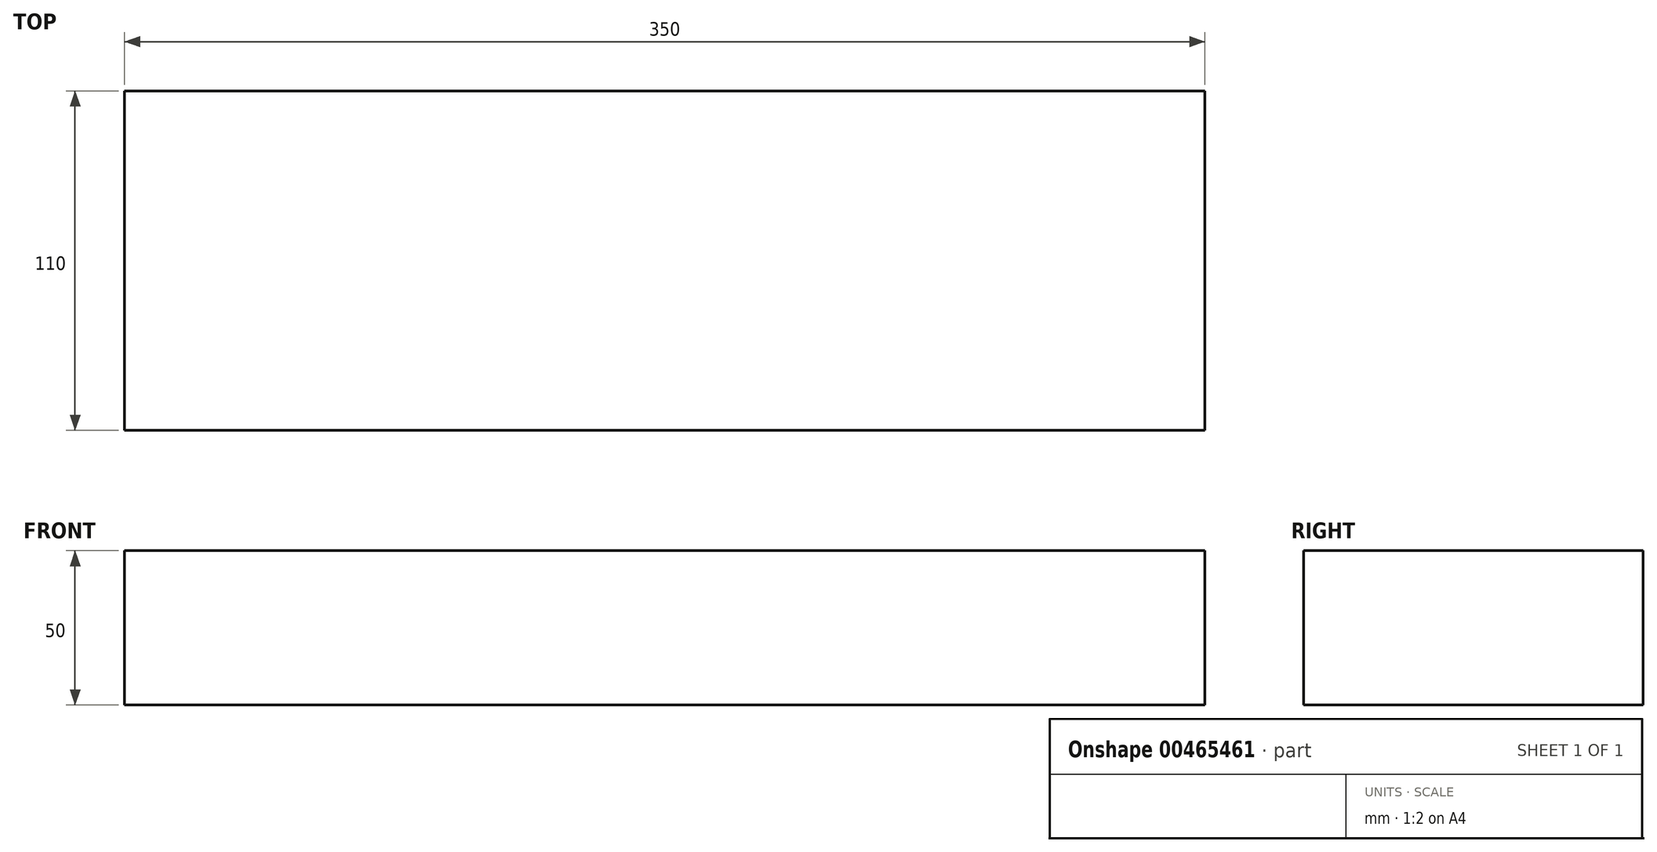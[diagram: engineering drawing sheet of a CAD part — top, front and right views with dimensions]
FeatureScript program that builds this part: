
annotation { "Feature Type Name" : "Feature", "Feature Type Description" : "" }
export const myFeature = defineFeature(function(context is Context, id is Id, definition is map)
    precondition{}
    {
        {
            var Q0;
            Q0=qCreatedBy(makeId("Top.planeOp"),FACE);
            var sketch = newSketch(context, id + "F0", { "sketchPlane" : qUnion([Q0])});
            skLineSegment(sketch, "E0.bottom", {"start": v(-509.87, -280.53) * mm, "end": v(-159.87, -280.53) * mm});
            skLineSegment(sketch, "E0.top", {"start": v(-509.87, -170.53) * mm, "end": v(-159.87, -170.53) * mm});
            skLineSegment(sketch, "E0.left", {"start": v(-509.87, -280.53) * mm, "end": v(-509.87, -170.53) * mm});
            skLineSegment(sketch, "E0.right", {"start": v(-159.87, -280.53) * mm, "end": v(-159.87, -170.53) * mm});
            skSolve(sketch);
        }
        {
            var Q0;
            Q0=qSketchRegion(id+"F0",true);
            extrude(context, id + "F1", {"entities" : qUnion([Q0]), "depth" : 50 * mm});
        }
    });
